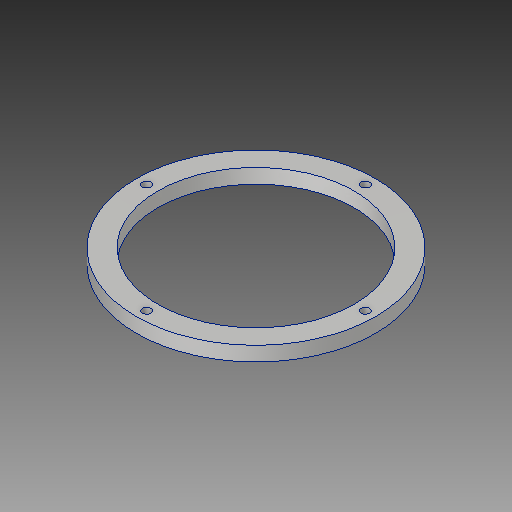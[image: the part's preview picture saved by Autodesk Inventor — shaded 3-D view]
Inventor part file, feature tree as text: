
AUTODESK INVENTOR PART (.ipt)
format: ipt  version: 2019 (Build 230136000, 136)  size: 103,424 bytes
history: native  units: mm
features: sketch x2, other x1, extrude x1, hole x1
ambient origin geometry x8: Origin, YZ Plane, XZ Plane, XY Plane, X Axis, Y Axis, Z Axis, Center Point
bodies: Body1 (feature_tree)
feature tree (5):
  other  "ソリッド1"
  extrude  "押し出し1"  Depth=115.0mm
  hole  "穴1"  [1 undecoded]
  sketch  "スケッチ1"
  sketch  "スケッチ2"
note: 1 required parameter value undecoded (feature->parameter linkage not recoverable at this tier; creation-order binding heuristic only, values carry confidence <= 0.55)
